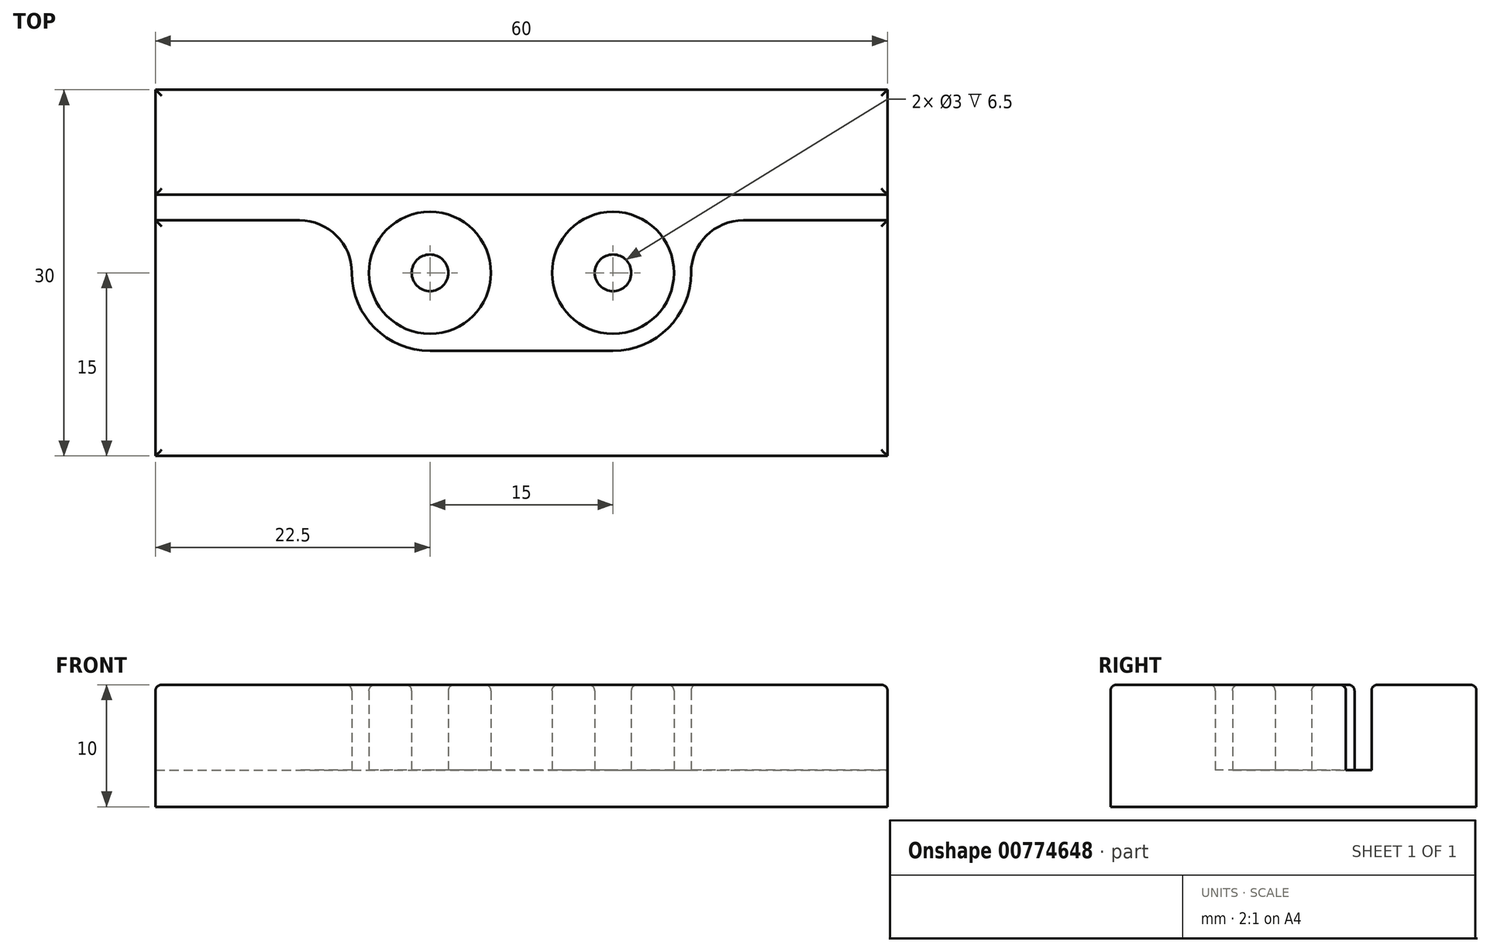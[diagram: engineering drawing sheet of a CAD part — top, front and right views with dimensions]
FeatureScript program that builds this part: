
annotation { "Feature Type Name" : "Feature", "Feature Type Description" : "" }
export const myFeature = defineFeature(function(context is Context, id is Id, definition is map)
    precondition{}
    {
        {
            var Q0;
            Q0=qCreatedBy(makeId("Top.planeOp"),FACE);
            var sketch = newSketch(context, id + "F0", { "sketchPlane" : qUnion([Q0])});
            skLineSegment(sketch, "E0.bottom", {"start": v(-30, 15) * mm, "end": v(30, 15) * mm});
            skLineSegment(sketch, "E0.top", {"start": v(-30, -15) * mm, "end": v(30, -15) * mm});
            skLineSegment(sketch, "E0.left", {"start": v(-30, 15) * mm, "end": v(-30, -15) * mm});
            skLineSegment(sketch, "E0.right", {"start": v(30, 15) * mm, "end": v(30, -15) * mm});
            skSolve(sketch);
        }
        {
            var Q0;
            Q0 = qSketchRegion(id + "F0", true);
            extrude(context, id + "F1", {"entities" : qUnion([Q0]), "depth" : 3 * mm, "offsetDistance" : 25 * mm});
        }
        {
            var Q0;
            Q0=makeQuery(id+"F1.opExtrude","CAP_FACE",FACE,{"disambiguationData":[OSD([sQuery(id+"F0.wireOp",EDGE,"E0.bottom"),sQuery(id+"F0.wireOp",EDGE,"E0.top"),sQuery(id+"F0.wireOp",EDGE,"E0.left"),sQuery(id+"F0.wireOp",EDGE,"E0.right")])],"isStart":false});
            var sketch = newSketch(context, id + "F2", { "sketchPlane" : qUnion([Q0])});
            skLineSegment(sketch, "E1", {"start": v(-30, 15) * mm, "end": v(-30, 6.4) * mm});
            skLineSegment(sketch, "E2", {"start": v(-30, 6.4) * mm, "end": v(30, 6.4) * mm});
            skLineSegment(sketch, "E3", {"start": v(30, 6.4) * mm, "end": v(30, 15) * mm});
            skLineSegment(sketch, "E4", {"start": v(30, 15) * mm, "end": v(-30, 15) * mm});
            skCircle(sketch, "E5", {"center": v(-7.5, 0) * mm, "radius": 5 * mm});
            skCircle(sketch, "E6", {"center": v(7.5, 0) * mm, "radius": 5 * mm});
            skLineSegment(sketch, "E7", {"start": v(-30, 4.3) * mm, "end": v(-18.2, 4.3) * mm});
            skLineSegment(sketch, "E8", {"start": v(-30, 4.3) * mm, "end": v(-30, -15) * mm});
            skLineSegment(sketch, "E9", {"start": v(-30, -15) * mm, "end": v(30, -15) * mm});
            skLineSegment(sketch, "E10", {"start": v(30, -15) * mm, "end": v(30, 4.3) * mm});
            skLineSegment(sketch, "E11", {"start": v(30, 4.3) * mm, "end": v(18.2, 4.3) * mm});
            skLineSegment(sketch, "E12", {"start": v(7.5, -6.4) * mm, "end": v(-7.5, -6.4) * mm});
            skArc(sketch, "E13", {"start": v(-7.5, -6.4) * mm, "mid": v(-12.03, -4.53) * mm, "end": v(-13.9, 0) * mm});
            skArc(sketch, "E14", {"start": v(7.5, -6.4) * mm, "mid": v(12.03, -4.53) * mm, "end": v(13.9, 0) * mm});
            skArc(sketch, "E15", {"start": v(-18.2, 4.3) * mm, "mid": v(-15.16, 3.04) * mm, "end": v(-13.9, 0) * mm});
            skArc(sketch, "E16", {"start": v(18.2, 4.3) * mm, "mid": v(15.16, 3.04) * mm, "end": v(13.9, 0) * mm});
            skCircle(sketch, "E17", {"center": v(-7.5, 0) * mm, "radius": 1.5 * mm});
            skCircle(sketch, "E18", {"center": v(7.5, 0) * mm, "radius": 1.5 * mm});
            skSolve(sketch);
        }
        {
            var Q0;
            Q0 = qSketchRegion(id + "F2", true);
            extrude(context, id + "F3", {"entities" : qUnion([Q0]), "operationType" : NewBodyOperationType.ADD, "depth" : 7 * mm, "offsetDistance" : 25 * mm});
        }
        {
            var Q0;
            Q0=makeQuery(id+"F3.opExtrude","CAP_FACE",FACE,{"disambiguationData":[OSD([sQuery(id+"F2.wireOp",EDGE,"E7"),sQuery(id+"F2.wireOp",EDGE,"E8"),sQuery(id+"F2.wireOp",EDGE,"E9"),sQuery(id+"F2.wireOp",EDGE,"E10"),sQuery(id+"F2.wireOp",EDGE,"E11"),sQuery(id+"F2.wireOp",EDGE,"E12"),sQuery(id+"F2.wireOp",EDGE,"E13"),sQuery(id+"F2.wireOp",EDGE,"E14"),sQuery(id+"F2.wireOp",EDGE,"E15"),sQuery(id+"F2.wireOp",EDGE,"E16")])],"isStart":false});
            var Q1;
            Q1=makeQuery(id+"F3.opExtrude","CAP_FACE",FACE,{"disambiguationData":[OSD([sQuery(id+"F2.wireOp",EDGE,"E1"),sQuery(id+"F2.wireOp",EDGE,"E2"),sQuery(id+"F2.wireOp",EDGE,"E3"),sQuery(id+"F2.wireOp",EDGE,"E4")])],"isStart":false});
            var Q2;
            Q2=makeQuery(id+"F3.opExtrude","CAP_FACE",FACE,{"disambiguationData":[OSD([sQuery(id+"F2.wireOp",EDGE,"E5")])],"isStart":false});
            var Q3;
            Q3=makeQuery(id+"F3.opExtrude","CAP_FACE",FACE,{"disambiguationData":[OSD([sQuery(id+"F2.wireOp",EDGE,"E6")])],"isStart":false});
            fillet(context, id + "F4", {"entities" : qUnion([Q0, Q1, Q2, Q3]), "tangentPropagation" : true, "radius" : 0.5 * mm, "defaultsChanged" : false, "vertexSettings" : [], "allowEdgeOverflow" : false});
        }
    });
